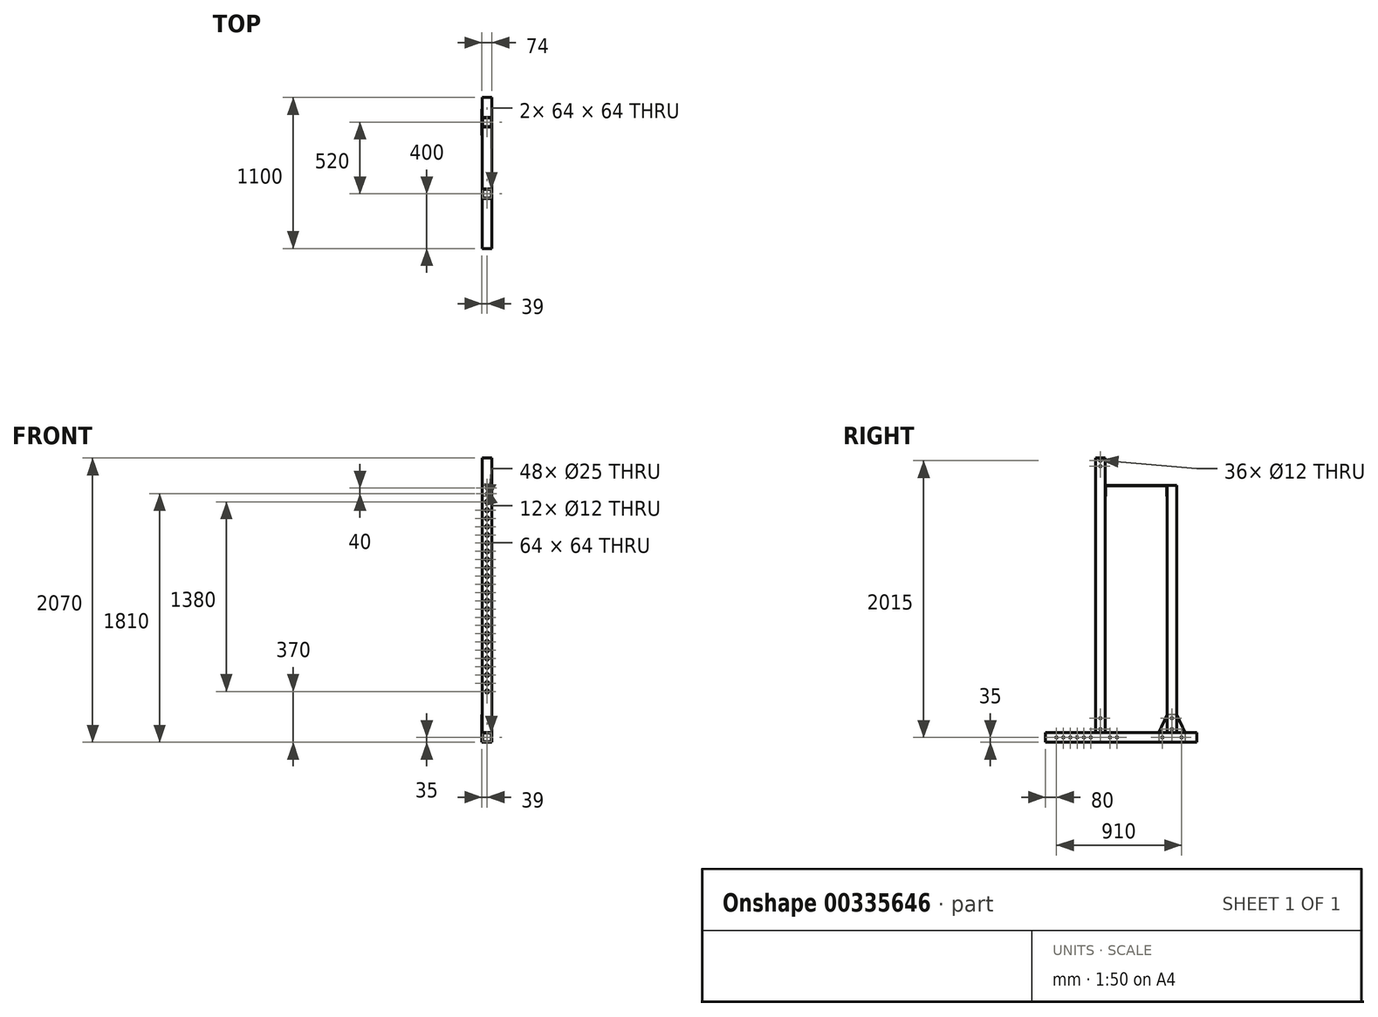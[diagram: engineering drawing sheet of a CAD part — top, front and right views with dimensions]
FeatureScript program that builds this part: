
annotation { "Feature Type Name" : "Feature", "Feature Type Description" : "" }
export const myFeature = defineFeature(function(context is Context, id is Id, definition is map)
    precondition{}
    {
        {
            var Q0;
            Q0=qCreatedBy(makeId("Front.planeOp"),FACE);
            var sketch = newSketch(context, id + "F0", { "sketchPlane" : qUnion([Q0])});
            skLineSegment(sketch, "E0.bottom", {"start": v(0, 0) * mm, "end": v(70, 0) * mm});
            skLineSegment(sketch, "E0.top", {"start": v(0, 70) * mm, "end": v(70, 70) * mm});
            skLineSegment(sketch, "E0.left", {"start": v(0, 0) * mm, "end": v(0, 70) * mm});
            skLineSegment(sketch, "E0.right", {"start": v(70, 0) * mm, "end": v(70, 70) * mm});
            skLineSegment(sketch, "E1.0", {"start": v(67, 3) * mm, "end": v(67, 67) * mm});
            skLineSegment(sketch, "E1.1", {"start": v(3, 3) * mm, "end": v(67, 3) * mm});
            skLineSegment(sketch, "E1.2", {"start": v(3, 3) * mm, "end": v(3, 67) * mm});
            skLineSegment(sketch, "E1.3", {"start": v(3, 67) * mm, "end": v(67, 67) * mm});
            skSolve(sketch);
        }
        {
            var Q0;
            Q0 = qSketchRegion(id + "F0", true);
            extrude(context, id + "F1", {"entities" : qUnion([Q0]), "oppositeDirection" : true, "depth" : 1100 * mm});
        }
        {
            var Q0;
            Q0=makeQuery(id+"F1.opExtrude","SWEPT_FACE",FACE,{"disambiguationData":[OSD([sQuery(id+"F0.wireOp",EDGE,"E0.left")])]});
            var sketch = newSketch(context, id + "F2", { "sketchPlane" : qUnion([Q0])});
            skLineSegment(sketch, "E2", {"start": v(-1100, 35) * mm, "end": v(0, 35) * mm, "construction": true});
            skCircle(sketch, "E3", {"center": v(-470, 35) * mm, "radius": 6 * mm});
            skCircle(sketch, "E4", {"center": v(-330, 35) * mm, "radius": 6 * mm});
            skCircle(sketch, "E5", {"center": v(-280, 35) * mm, "radius": 6 * mm, "construction": true});
            skCircle(sketch, "E6", {"center": v(-230, 35) * mm, "radius": 6 * mm});
            skCircle(sketch, "E7", {"center": v(-180, 35) * mm, "radius": 6 * mm, "construction": true});
            skCircle(sketch, "E8", {"center": v(-130, 35) * mm, "radius": 6 * mm});
            skCircle(sketch, "E9.MirrorC", {"center": v(-280, 35) * mm, "radius": 6 * mm});
            skCircle(sketch, "E10.MirrorC", {"center": v(-180, 35) * mm, "radius": 6 * mm});
            skCircle(sketch, "E11", {"center": v(-80, 35) * mm, "radius": 6 * mm});
            skCircle(sketch, "E12", {"center": v(-520, 35) * mm, "radius": 6 * mm});
            skCircle(sketch, "E13", {"center": v(-990, 35) * mm, "radius": 6 * mm});
            skCircle(sketch, "E14", {"center": v(-850, 35) * mm, "radius": 6 * mm});
            skPoint(sketch, "E15", {"position": v(-920, 70) * mm});
            skPoint(sketch, "E16", {"position": v(-400, 70) * mm});
            skSolve(sketch);
        }
        {
            var Q0;
            Q0=sQuery(id+"F2.wireOp",VERTEX,"E13.center");
            var Q1;
            Q1=sQuery(id+"F2.wireOp",VERTEX,"E14.center");
            var Q2;
            Q2=sQuery(id+"F2.wireOp",VERTEX,"E12.center");
            var Q3;
            Q3=sQuery(id+"F2.wireOp",VERTEX,"E3.center");
            var Q4;
            Q4=sQuery(id+"F2.wireOp",VERTEX,"E4.center");
            var Q5;
            Q5=sQuery(id+"F2.wireOp",VERTEX,"E9.MirrorC.center");
            var Q6;
            Q6=sQuery(id+"F2.wireOp",VERTEX,"E6.center");
            var Q7;
            Q7=sQuery(id+"F2.wireOp",VERTEX,"E10.MirrorC.center");
            var Q8;
            Q8=sQuery(id+"F2.wireOp",VERTEX,"E8.center");
            var Q9;
            Q9=sQuery(id+"F2.wireOp",VERTEX,"E11.center");
            var Q10;
            Q10=makeQuery(id+"F1.opExtrude","SWEPT_BODY",BODY,{"disambiguationData":[OSD([sQuery(id+"F0.wireOp",EDGE,"E0.bottom"),sQuery(id+"F0.wireOp",EDGE,"E0.top"),sQuery(id+"F0.wireOp",EDGE,"E0.left"),sQuery(id+"F0.wireOp",EDGE,"E0.right"),sQuery(id+"F0.wireOp",EDGE,"E1.0"),sQuery(id+"F0.wireOp",EDGE,"E1.1"),sQuery(id+"F0.wireOp",EDGE,"E1.2"),sQuery(id+"F0.wireOp",EDGE,"E1.3")])]});
            hole(context, id + "F3", {"style" : HoleStyle.SIMPLE, "endStyle" : HoleEndStyle.THROUGH, "holeDiameter" : 12 * mm, "isTappedThrough" : true, "tappedDepth" : 12 * mm, "tapClearance" : 3, "locations" : qUnion([Q0, Q1, Q2, Q3, Q4, Q5, Q6, Q7, Q8, Q9]), "scope" : qUnion([Q10])});
        }
        {
            var Q0;
            Q0=makeQuery(id+"F1.opExtrude","SWEPT_FACE",FACE,{"disambiguationData":[OSD([sQuery(id+"F0.wireOp",EDGE,"E0.top")])]});
            var sketch = newSketch(context, id + "F4", { "sketchPlane" : qUnion([Q0])});
            skLineSegment(sketch, "E17.bottom", {"start": v(0, 435) * mm, "end": v(70, 435) * mm});
            skLineSegment(sketch, "E17.top", {"start": v(0, 365) * mm, "end": v(70, 365) * mm});
            skLineSegment(sketch, "E17.left", {"start": v(0, 435) * mm, "end": v(0, 365) * mm});
            skLineSegment(sketch, "E17.right", {"start": v(70, 435) * mm, "end": v(70, 365) * mm});
            skLineSegment(sketch, "E18", {"start": v(35, 435) * mm, "end": v(35, 365) * mm, "construction": true});
            skLineSegment(sketch, "E19", {"start": v(0, 400) * mm, "end": v(70, 400) * mm, "construction": true});
            skPoint(sketch, "E20", {"position": v(35, 400) * mm});
            skLineSegment(sketch, "E21.0", {"start": v(3, 432) * mm, "end": v(67, 432) * mm});
            skLineSegment(sketch, "E21.1", {"start": v(3, 432) * mm, "end": v(3, 368) * mm});
            skLineSegment(sketch, "E21.2", {"start": v(3, 368) * mm, "end": v(67, 368) * mm});
            skLineSegment(sketch, "E21.3", {"start": v(67, 432) * mm, "end": v(67, 368) * mm});
            skSolve(sketch);
        }
        {
            var Q0;
            Q0 = qSketchRegion(id + "F4", true);
            extrude(context, id + "F5", {"entities" : qUnion([Q0]), "depth" : 2000 * mm});
        }
        {
            var Q0;
            Q0=makeQuery(id+"F5.opExtrude","SWEPT_FACE",FACE,{"disambiguationData":[OSD([sQuery(id+"F4.wireOp",EDGE,"E17.top")])]});
            var sketch = newSketch(context, id + "F6", { "sketchPlane" : qUnion([Q0])});
            skLineSegment(sketch, "E22", {"start": v(35, 2070) * mm, "end": v(35, 70) * mm, "construction": true});
            skCircle(sketch, "E23", {"center": v(35, 370) * mm, "radius": 12.5 * mm});
            skCircle(sketch, "E24.0.1.0", {"center": v(35, 430) * mm, "radius": 12.5 * mm});
            skCircle(sketch, "E24.0.2.0", {"center": v(35, 490) * mm, "radius": 12.5 * mm});
            skCircle(sketch, "E24.0.3.0", {"center": v(35, 550) * mm, "radius": 12.5 * mm});
            skCircle(sketch, "E24.0.4.0", {"center": v(35, 610) * mm, "radius": 12.5 * mm});
            skCircle(sketch, "E24.0.5.0", {"center": v(35, 670) * mm, "radius": 12.5 * mm});
            skCircle(sketch, "E24.0.6.0", {"center": v(35, 730) * mm, "radius": 12.5 * mm});
            skCircle(sketch, "E24.0.7.0", {"center": v(35, 790) * mm, "radius": 12.5 * mm});
            skCircle(sketch, "E24.0.8.0", {"center": v(35, 850) * mm, "radius": 12.5 * mm});
            skCircle(sketch, "E24.0.9.0", {"center": v(35, 910) * mm, "radius": 12.5 * mm});
            skCircle(sketch, "E24.0.10.0", {"center": v(35, 970) * mm, "radius": 12.5 * mm});
            skCircle(sketch, "E24.0.11.0", {"center": v(35, 1030) * mm, "radius": 12.5 * mm});
            skCircle(sketch, "E24.0.12.0", {"center": v(35, 1090) * mm, "radius": 12.5 * mm});
            skCircle(sketch, "E24.0.13.0", {"center": v(35, 1150) * mm, "radius": 12.5 * mm});
            skCircle(sketch, "E24.0.14.0", {"center": v(35, 1210) * mm, "radius": 12.5 * mm});
            skLineSegment(sketch, "E24.direction1", {"start": v(35, 370) * mm, "end": v(60, 370) * mm, "construction": true});
            skLineSegment(sketch, "E24.direction2", {"start": v(35, 370) * mm, "end": v(35, 430) * mm, "construction": true});
            skCircle(sketch, "E25.0.0.15", {"center": v(35, 1270) * mm, "radius": 12.5 * mm});
            skCircle(sketch, "E25.0.0.16", {"center": v(35, 1330) * mm, "radius": 12.5 * mm});
            skCircle(sketch, "E25.0.0.17", {"center": v(35, 1390) * mm, "radius": 12.5 * mm});
            skCircle(sketch, "E25.0.0.18", {"center": v(35, 1450) * mm, "radius": 12.5 * mm});
            skCircle(sketch, "E25.0.0.19", {"center": v(35, 1510) * mm, "radius": 12.5 * mm});
            skCircle(sketch, "E26.0.0.20", {"center": v(35, 1570) * mm, "radius": 12.5 * mm});
            skCircle(sketch, "E26.0.0.21", {"center": v(35, 1630) * mm, "radius": 12.5 * mm});
            skCircle(sketch, "E26.0.0.22", {"center": v(35, 1690) * mm, "radius": 12.5 * mm});
            skCircle(sketch, "E27.0.0.23", {"center": v(35, 1750) * mm, "radius": 12.5 * mm});
            skSolve(sketch);
        }
        {
            var Q0;
            Q0=sQuery(id+"F6.wireOp",VERTEX,"31c33e48-db0a-453b-9812-984305228cee.0.0.20.center");
            var Q1;
            Q1=sQuery(id+"F6.wireOp",VERTEX,"E25.0.0.19.center");
            var Q2;
            Q2=sQuery(id+"F6.wireOp",VERTEX,"E25.0.0.18.center");
            var Q3;
            Q3=sQuery(id+"F6.wireOp",VERTEX,"E25.0.0.17.center");
            var Q4;
            Q4=sQuery(id+"F6.wireOp",VERTEX,"E25.0.0.16.center");
            var Q5;
            Q5=sQuery(id+"F6.wireOp",VERTEX,"E25.0.0.15.center");
            var Q6;
            Q6=sQuery(id+"F6.wireOp",VERTEX,"E24.0.14.0.center");
            var Q7;
            Q7=sQuery(id+"F6.wireOp",VERTEX,"E24.0.13.0.center");
            var Q8;
            Q8=sQuery(id+"F6.wireOp",VERTEX,"E24.0.12.0.center");
            var Q9;
            Q9=sQuery(id+"F6.wireOp",VERTEX,"E24.0.11.0.center");
            var Q10;
            Q10=sQuery(id+"F6.wireOp",VERTEX,"E24.0.10.0.center");
            var Q11;
            Q11=sQuery(id+"F6.wireOp",VERTEX,"E24.0.9.0.center");
            var Q12;
            Q12=sQuery(id+"F6.wireOp",VERTEX,"E24.0.8.0.center");
            var Q13;
            Q13=sQuery(id+"F6.wireOp",VERTEX,"E24.0.7.0.center");
            var Q14;
            Q14=sQuery(id+"F6.wireOp",VERTEX,"E24.0.6.0.center");
            var Q15;
            Q15=sQuery(id+"F6.wireOp",VERTEX,"E24.0.5.0.center");
            var Q16;
            Q16=sQuery(id+"F6.wireOp",VERTEX,"E24.0.4.0.center");
            var Q17;
            Q17=sQuery(id+"F6.wireOp",VERTEX,"E24.0.3.0.center");
            var Q18;
            Q18=sQuery(id+"F6.wireOp",VERTEX,"E24.0.2.0.center");
            var Q19;
            Q19=sQuery(id+"F6.wireOp",VERTEX,"E24.0.1.0.center");
            var Q20;
            Q20=sQuery(id+"F6.wireOp",VERTEX,"E23.center");
            var Q21;
            Q21=sQuery(id+"F6.wireOp",VERTEX,"E26.0.0.20.center");
            var Q22;
            Q22=sQuery(id+"F6.wireOp",VERTEX,"E26.0.0.21.center");
            var Q23;
            Q23=sQuery(id+"F6.wireOp",VERTEX,"E26.0.0.22.center");
            var Q24;
            Q24=sQuery(id+"F6.wireOp",VERTEX,"E27.0.0.23.center");
            var Q25;
            Q25=makeQuery(id+"F5.opExtrude","SWEPT_BODY",BODY,{"disambiguationData":[OSD([sQuery(id+"F4.wireOp",EDGE,"E17.bottom"),sQuery(id+"F4.wireOp",EDGE,"E17.top"),sQuery(id+"F4.wireOp",EDGE,"E17.left"),sQuery(id+"F4.wireOp",EDGE,"E17.right"),sQuery(id+"F4.wireOp",EDGE,"E21.0"),sQuery(id+"F4.wireOp",EDGE,"E21.1"),sQuery(id+"F4.wireOp",EDGE,"E21.2"),sQuery(id+"F4.wireOp",EDGE,"E21.3")])]});
            hole(context, id + "F7", {"style" : HoleStyle.SIMPLE, "endStyle" : HoleEndStyle.THROUGH, "holeDiameter" : 25 * mm, "isTappedThrough" : true, "tappedDepth" : 12 * mm, "tapClearance" : 3, "locations" : qUnion([Q0, Q1, Q2, Q3, Q4, Q5, Q6, Q7, Q8, Q9, Q10, Q11, Q12, Q13, Q14, Q15, Q16, Q17, Q18, Q19, Q20, Q21, Q22, Q23, Q24]), "scope" : qUnion([Q25])});
        }
        {
            var Q0;
            Q0=makeQuery(id+"F1.opExtrude","SWEPT_FACE",FACE,{"disambiguationData":[OSD([sQuery(id+"F0.wireOp",EDGE,"E0.top")])]});
            var sketch = newSketch(context, id + "F8", { "sketchPlane" : qUnion([Q0])});
            skLineSegment(sketch, "E28.bottom", {"start": v(70, 955) * mm, "end": v(0, 955) * mm});
            skLineSegment(sketch, "E28.top", {"start": v(70, 885) * mm, "end": v(0, 885) * mm});
            skLineSegment(sketch, "E28.left", {"start": v(70, 955) * mm, "end": v(70, 885) * mm});
            skLineSegment(sketch, "E28.right", {"start": v(0, 955) * mm, "end": v(0, 885) * mm});
            skLineSegment(sketch, "E29", {"start": v(70, 920) * mm, "end": v(0, 920) * mm, "construction": true});
            skPoint(sketch, "E30", {"position": v(35, 920) * mm});
            skLineSegment(sketch, "E31.0", {"start": v(67, 952) * mm, "end": v(67, 888) * mm});
            skLineSegment(sketch, "E31.1", {"start": v(67, 952) * mm, "end": v(3, 952) * mm});
            skLineSegment(sketch, "E31.2", {"start": v(3, 952) * mm, "end": v(3, 888) * mm});
            skLineSegment(sketch, "E31.3", {"start": v(67, 888) * mm, "end": v(3, 888) * mm});
            skSolve(sketch);
        }
        {
            var Q0;
            Q0 = qSketchRegion(id + "F8", true);
            extrude(context, id + "F9", {"entities" : qUnion([Q0]), "depth" : 1800 * mm});
        }
        {
            var Q0;
            Q0=makeQuery(id+"F5.opExtrude","SWEPT_FACE",FACE,{"disambiguationData":[OSD([sQuery(id+"F4.wireOp",EDGE,"E17.left")])]});
            var sketch = newSketch(context, id + "F10", { "sketchPlane" : qUnion([Q0])});
            skLineSegment(sketch, "E32.0", {"start": v(-365, 1762.5) * mm, "end": v(-365, 1737.5) * mm});
            skLineSegment(sketch, "E33.0", {"start": v(-885, 1870) * mm, "end": v(-885, 70) * mm});
            skLineSegment(sketch, "E34", {"start": v(-885, 1870) * mm, "end": v(-435, 1870) * mm});
            skLineSegment(sketch, "E35", {"start": v(-435, 1870) * mm, "end": v(-435, 1790) * mm});
            skLineSegment(sketch, "E36", {"start": v(-885, 1870) * mm, "end": v(-885, 1790) * mm});
            skLineSegment(sketch, "E37", {"start": v(-365, 1762.5) * mm, "end": v(-435, 1762.5) * mm, "construction": true});
            skLineSegment(sketch, "E38.0", {"start": v(-881, 1866) * mm, "end": v(-881, 1790) * mm});
            skLineSegment(sketch, "E38.1", {"start": v(-881, 1866) * mm, "end": v(-439, 1866) * mm});
            skLineSegment(sketch, "E38.2", {"start": v(-439, 1866) * mm, "end": v(-439, 1790) * mm});
            skLineSegment(sketch, "E39", {"start": v(-885, 1790) * mm, "end": v(-881, 1790) * mm});
            skLineSegment(sketch, "E40", {"start": v(-439, 1790) * mm, "end": v(-435, 1790) * mm});
            skSolve(sketch);
        }
        {
            var Q0;
            Q0 = qSketchRegion(id + "F10", true);
            extrude(context, id + "F11", {"entities" : qUnion([Q0]), "oppositeDirection" : true, "depth" : 70 * mm});
        }
        {
            var Q0;
            Q0=makeQuery(id+"F11.opExtrude","SWEPT_FACE",FACE,{"disambiguationData":[OSD([sQuery(id+"F10.wireOp",EDGE,"E38.0")])]});
            var sketch = newSketch(context, id + "F12", { "sketchPlane" : qUnion([Q0])});
            skLineSegment(sketch, "E41", {"start": v(35, 1790) * mm, "end": v(35, 1866) * mm, "construction": true});
            skCircle(sketch, "E42", {"center": v(35, 1810) * mm, "radius": 6 * mm});
            skCircle(sketch, "E43", {"center": v(35, 1850) * mm, "radius": 6 * mm});
            skSolve(sketch);
        }
        {
            var Q0;
            Q0=sQuery(id+"F12.wireOp",VERTEX,"E43.center");
            var Q1;
            Q1=sQuery(id+"F12.wireOp",VERTEX,"E42.center");
            var Q2;
            Q2=makeQuery(id+"F11.opExtrude","SWEPT_BODY",BODY,{"disambiguationData":[OSD([sQuery(id+"F10.wireOp",EDGE,"E34"),sQuery(id+"F10.wireOp",EDGE,"E35"),sQuery(id+"F10.wireOp",EDGE,"E36"),sQuery(id+"F10.wireOp",EDGE,"E38.0"),sQuery(id+"F10.wireOp",EDGE,"E38.1"),sQuery(id+"F10.wireOp",EDGE,"E38.2"),sQuery(id+"F10.wireOp",EDGE,"E39"),sQuery(id+"F10.wireOp",EDGE,"E40")])]});
            var Q3;
            Q3=makeQuery(id+"F9.opExtrude","SWEPT_BODY",BODY,{"disambiguationData":[OSD([sQuery(id+"F8.wireOp",EDGE,"E28.bottom"),sQuery(id+"F8.wireOp",EDGE,"E28.top"),sQuery(id+"F8.wireOp",EDGE,"E28.left"),sQuery(id+"F8.wireOp",EDGE,"E28.right"),sQuery(id+"F8.wireOp",EDGE,"E31.0"),sQuery(id+"F8.wireOp",EDGE,"E31.1"),sQuery(id+"F8.wireOp",EDGE,"E31.2"),sQuery(id+"F8.wireOp",EDGE,"E31.3")])]});
            hole(context, id + "F13", {"style" : HoleStyle.SIMPLE, "endStyle" : HoleEndStyle.THROUGH, "holeDiameter" : 12 * mm, "isTappedThrough" : true, "tappedDepth" : 12 * mm, "tapClearance" : 3, "locations" : qUnion([Q0, Q1]), "scope" : qUnion([Q2, Q3])});
        }
        {
            var Q0;
            Q0=makeQuery(id+"F11.opExtrude","SWEPT_FACE",FACE,{"disambiguationData":[OSD([sQuery(id+"F10.wireOp",EDGE,"E38.2")])]});
            var sketch = newSketch(context, id + "F14", { "sketchPlane" : qUnion([Q0])});
            skLineSegment(sketch, "E44", {"start": v(-35, 1790) * mm, "end": v(-35, 1866) * mm, "construction": true});
            skCircle(sketch, "E45", {"center": v(-35, 1810) * mm, "radius": 6 * mm});
            skCircle(sketch, "E46", {"center": v(-35, 1850) * mm, "radius": 6 * mm});
            skSolve(sketch);
        }
        {
            var Q0;
            Q0=sQuery(id+"F14.wireOp",VERTEX,"E46.center");
            var Q1;
            Q1=sQuery(id+"F14.wireOp",VERTEX,"E45.center");
            var Q2;
            Q2=makeQuery(id+"F5.opExtrude","SWEPT_BODY",BODY,{"disambiguationData":[OSD([sQuery(id+"F4.wireOp",EDGE,"E17.bottom"),sQuery(id+"F4.wireOp",EDGE,"E17.top"),sQuery(id+"F4.wireOp",EDGE,"E17.left"),sQuery(id+"F4.wireOp",EDGE,"E17.right"),sQuery(id+"F4.wireOp",EDGE,"E21.0"),sQuery(id+"F4.wireOp",EDGE,"E21.1"),sQuery(id+"F4.wireOp",EDGE,"E21.2"),sQuery(id+"F4.wireOp",EDGE,"E21.3")])]});
            var Q3;
            Q3=makeQuery(id+"F11.opExtrude","SWEPT_BODY",BODY,{"disambiguationData":[OSD([sQuery(id+"F10.wireOp",EDGE,"E34"),sQuery(id+"F10.wireOp",EDGE,"E35"),sQuery(id+"F10.wireOp",EDGE,"E36"),sQuery(id+"F10.wireOp",EDGE,"E38.0"),sQuery(id+"F10.wireOp",EDGE,"E38.1"),sQuery(id+"F10.wireOp",EDGE,"E38.2"),sQuery(id+"F10.wireOp",EDGE,"E39"),sQuery(id+"F10.wireOp",EDGE,"E40")])]});
            hole(context, id + "F15", {"style" : HoleStyle.SIMPLE, "endStyle" : HoleEndStyle.THROUGH, "holeDiameter" : 12 * mm, "isTappedThrough" : true, "tappedDepth" : 12 * mm, "tapClearance" : 3, "locations" : qUnion([Q0, Q1]), "scope" : qUnion([Q2, Q3])});
        }
        {
            var Q0;
            Q0=makeQuery(id+"F1.opExtrude","SWEPT_FACE",FACE,{"disambiguationData":[OSD([sQuery(id+"F0.wireOp",EDGE,"E0.left")])]});
            var sketch = newSketch(context, id + "F16", { "sketchPlane" : qUnion([Q0])});
            skLineSegment(sketch, "E47", {"start": v(-990, 35) * mm, "end": v(-850, 35) * mm, "construction": true});
            skLineSegment(sketch, "E48", {"start": v(-1015, 70) * mm, "end": v(-1015, 0) * mm});
            skLineSegment(sketch, "E49", {"start": v(-825, 70) * mm, "end": v(-825, 0) * mm});
            skPoint(sketch, "E50", {"position": v(-920, 35) * mm});
            skLineSegment(sketch, "E51.0.0", {"start": v(-955, 70) * mm, "end": v(-885, 70) * mm});
            skLineSegment(sketch, "E51.0.1", {"start": v(-885, 70) * mm, "end": v(-885, 200) * mm});
            skLineSegment(sketch, "E51.0.2", {"start": v(-885, 1870) * mm, "end": v(-955, 1870) * mm});
            skLineSegment(sketch, "E51.0.3", {"start": v(-955, 200) * mm, "end": v(-955, 70) * mm});
            skLineSegment(sketch, "E52", {"start": v(-1015, 0) * mm, "end": v(-825, 0) * mm});
            skLineSegment(sketch, "E53", {"start": v(-955, 200) * mm, "end": v(-885, 200) * mm});
            skPoint(sketch, "E54", {"position": v(-920, 0) * mm});
            skLineSegment(sketch, "E55", {"start": v(-1015, 70) * mm, "end": v(-955, 200) * mm});
            skLineSegment(sketch, "E56", {"start": v(-825, 70) * mm, "end": v(-885, 200) * mm});
            skLineSegment(sketch, "E57", {"start": v(-920, 0) * mm, "end": v(-920, 200) * mm, "construction": true});
            skCircle(sketch, "E58", {"center": v(-920, 175) * mm, "radius": 6 * mm});
            skCircle(sketch, "E59", {"center": v(-920, 95) * mm, "radius": 6 * mm});
            skCircle(sketch, "E60", {"center": v(-990, 35) * mm, "radius": 6 * mm});
            skCircle(sketch, "E61", {"center": v(-850, 35) * mm, "radius": 6 * mm});
            skSolve(sketch);
        }
        {
            var Q0;
            Q0 = qSketchRegion(id + "F16", true);
            extrude(context, id + "F17", {"entities" : qUnion([Q0]), "depth" : 4 * mm});
        }
        {
            var Q0;
            Q0=makeQuery(id+"F9.opExtrude","SWEPT_FACE",FACE,{"disambiguationData":[OSD([sQuery(id+"F8.wireOp",EDGE,"E28.right")])]});
            var sketch = newSketch(context, id + "F18", { "sketchPlane" : qUnion([Q0])});
            skCircle(sketch, "E62.0", {"center": v(-920, 175) * mm, "radius": 6 * mm});
            skCircle(sketch, "E63.0", {"center": v(-920, 95) * mm, "radius": 6 * mm});
            skLineSegment(sketch, "E64", {"start": v(-920, 1870) * mm, "end": v(-920, 70) * mm, "construction": true});
            skSolve(sketch);
        }
        {
            var Q0;
            Q0=sQuery(id+"F18.wireOp",VERTEX,"E62.0.center");
            var Q1;
            Q1=sQuery(id+"F18.wireOp",VERTEX,"E63.0.center");
            var Q2;
            Q2=makeQuery(id+"F9.opExtrude","SWEPT_BODY",BODY,{"disambiguationData":[OSD([sQuery(id+"F8.wireOp",EDGE,"E28.bottom"),sQuery(id+"F8.wireOp",EDGE,"E28.top"),sQuery(id+"F8.wireOp",EDGE,"E28.left"),sQuery(id+"F8.wireOp",EDGE,"E28.right"),sQuery(id+"F8.wireOp",EDGE,"E31.0"),sQuery(id+"F8.wireOp",EDGE,"E31.1"),sQuery(id+"F8.wireOp",EDGE,"E31.2"),sQuery(id+"F8.wireOp",EDGE,"E31.3")])]});
            hole(context, id + "F19", {"style" : HoleStyle.SIMPLE, "endStyle" : HoleEndStyle.THROUGH, "holeDiameter" : 12 * mm, "isTappedThrough" : true, "tappedDepth" : 12 * mm, "tapClearance" : 3, "locations" : qUnion([Q0, Q1]), "scope" : qUnion([Q2])});
        }
        {
            var Q0;
            Q0=makeQuery(id+"F5.opExtrude","SWEPT_FACE",FACE,{"disambiguationData":[OSD([sQuery(id+"F4.wireOp",EDGE,"E17.left")])]});
            var sketch = newSketch(context, id + "F20", { "sketchPlane" : qUnion([Q0])});
            skLineSegment(sketch, "E65", {"start": v(-400, 70) * mm, "end": v(-400, 2070) * mm, "construction": true});
            skCircle(sketch, "E66", {"center": v(-400, 95) * mm, "radius": 6 * mm});
            skCircle(sketch, "E67", {"center": v(-400, 175) * mm, "radius": 6 * mm});
            skLineSegment(sketch, "E68", {"start": v(-435, 2066) * mm, "end": v(-365, 2066) * mm, "construction": true});
            skLineSegment(sketch, "E69", {"start": v(-435, 1990) * mm, "end": v(-365, 1990) * mm, "construction": true});
            skCircle(sketch, "E70", {"center": v(-400, 2010) * mm, "radius": 6 * mm});
            skCircle(sketch, "E71", {"center": v(-400, 2050) * mm, "radius": 6 * mm});
            skSolve(sketch);
        }
        {
            var Q0;
            Q0=sQuery(id+"F20.wireOp",VERTEX,"E71.center");
            var Q1;
            Q1=sQuery(id+"F20.wireOp",VERTEX,"E70.center");
            var Q2;
            Q2=sQuery(id+"F20.wireOp",VERTEX,"E67.center");
            var Q3;
            Q3=sQuery(id+"F20.wireOp",VERTEX,"E66.center");
            var Q4;
            Q4=makeQuery(id+"F5.opExtrude","SWEPT_BODY",BODY,{"disambiguationData":[OSD([sQuery(id+"F4.wireOp",EDGE,"E17.bottom"),sQuery(id+"F4.wireOp",EDGE,"E17.top"),sQuery(id+"F4.wireOp",EDGE,"E17.left"),sQuery(id+"F4.wireOp",EDGE,"E17.right"),sQuery(id+"F4.wireOp",EDGE,"E21.0"),sQuery(id+"F4.wireOp",EDGE,"E21.1"),sQuery(id+"F4.wireOp",EDGE,"E21.2"),sQuery(id+"F4.wireOp",EDGE,"E21.3")])]});
            hole(context, id + "F21", {"style" : HoleStyle.SIMPLE, "endStyle" : HoleEndStyle.THROUGH, "holeDiameter" : 12 * mm, "isTappedThrough" : true, "tappedDepth" : 12 * mm, "tapClearance" : 3, "locations" : qUnion([Q0, Q1, Q2, Q3]), "scope" : qUnion([Q4])});
        }
        {
            var Q0;
            Q0=makeQuery(id+"F5.opExtrude","SWEPT_FACE",FACE,{"disambiguationData":[OSD([sQuery(id+"F4.wireOp",EDGE,"E17.top")])]});
            var sketch = newSketch(context, id + "F22", { "sketchPlane" : qUnion([Q0])});
            skCircle(sketch, "E72.0", {"center": v(35, 1850) * mm, "radius": 6 * mm});
            skCircle(sketch, "E73.0", {"center": v(35, 1810) * mm, "radius": 6 * mm});
            skSolve(sketch);
        }
    });
